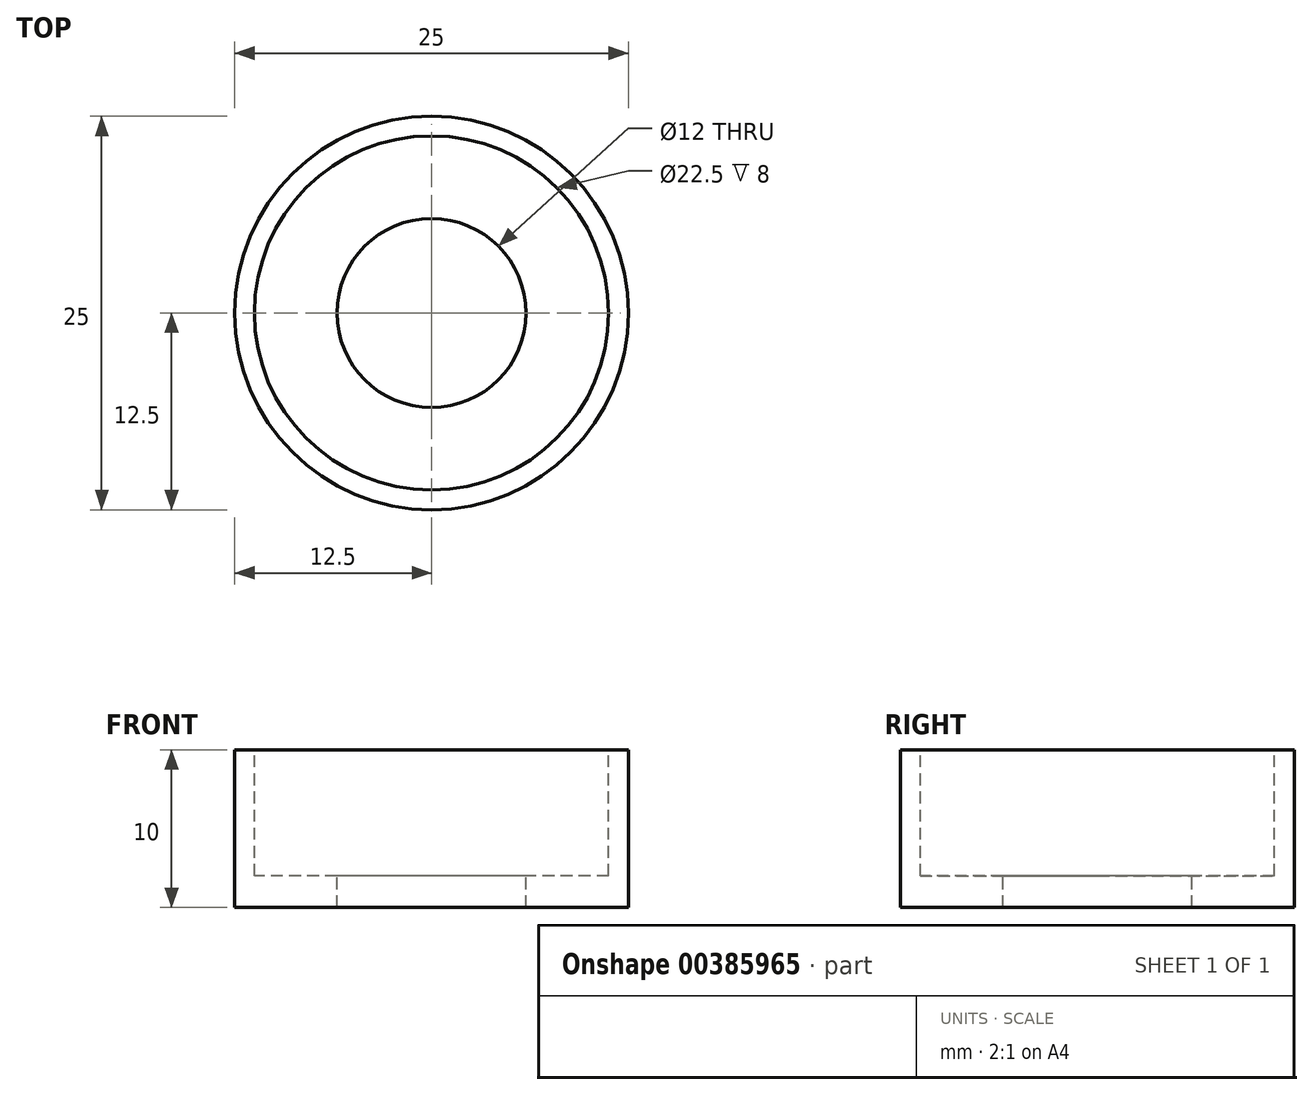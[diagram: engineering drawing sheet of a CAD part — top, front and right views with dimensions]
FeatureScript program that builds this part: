
annotation { "Feature Type Name" : "Feature", "Feature Type Description" : "" }
export const myFeature = defineFeature(function(context is Context, id is Id, definition is map)
    precondition{}
    {
        {
            var Q0;
            Q0=qCreatedBy(makeId("Top.planeOp"),FACE);
            var sketch = newSketch(context, id + "F0", { "sketchPlane" : qUnion([Q0])});
            skCircle(sketch, "E0", {"center": v(0, 0) * mm, "radius": 12.5 * mm});
            skSolve(sketch);
        }
        {
            var Q0;
            Q0 = qSketchRegion(id + "F0", true);
            extrude(context, id + "F1", {"entities" : qUnion([Q0]), "depth" : 10 * mm, "offsetDistance" : 25 * mm});
        }
        {
            var Q0;
            Q0=makeQuery(id+"F1.opExtrude","CAP_FACE",FACE,{"disambiguationData":[OSD([sQuery(id+"F0.wireOp",EDGE,"E0")])],"isStart":false});
            var sketch = newSketch(context, id + "F2", { "sketchPlane" : qUnion([Q0])});
            skCircle(sketch, "E1", {"center": v(0, 0) * mm, "radius": 11.25 * mm});
            skCircle(sketch, "E2", {"center": v(0, 0) * mm, "radius": 6 * mm});
            skSolve(sketch);
        }
        {
            var Q0;
            Q0=makeQuery(id+"F2.imprint","IMPRINT",FACE,{"disambiguationData":[TD([[makeQuery(id+"F2.imprint","IMPRINT",EDGE,{"derivedFrom":sQuery(id+"F2.wireOp",EDGE,"E2")}),1.0]])]});
            extrude(context, id + "F3", {"entities" : qUnion([Q0]), "operationType" : NewBodyOperationType.REMOVE, "oppositeDirection" : true, "depth" : 25 * mm, "offsetDistance" : 25 * mm});
        }
        {
            var Q0;
            Q0=makeQuery(id+"F2.imprint","IMPRINT",FACE,{"disambiguationData":[TD([[makeQuery(id+"F2.imprint","IMPRINT",EDGE,{"derivedFrom":sQuery(id+"F2.wireOp",EDGE,"E1")}),1.0]])]});
            extrude(context, id + "F4", {"entities" : qUnion([Q0]), "operationType" : NewBodyOperationType.REMOVE, "oppositeDirection" : true, "depth" : 8 * mm, "offsetDistance" : 25 * mm});
        }
    });
